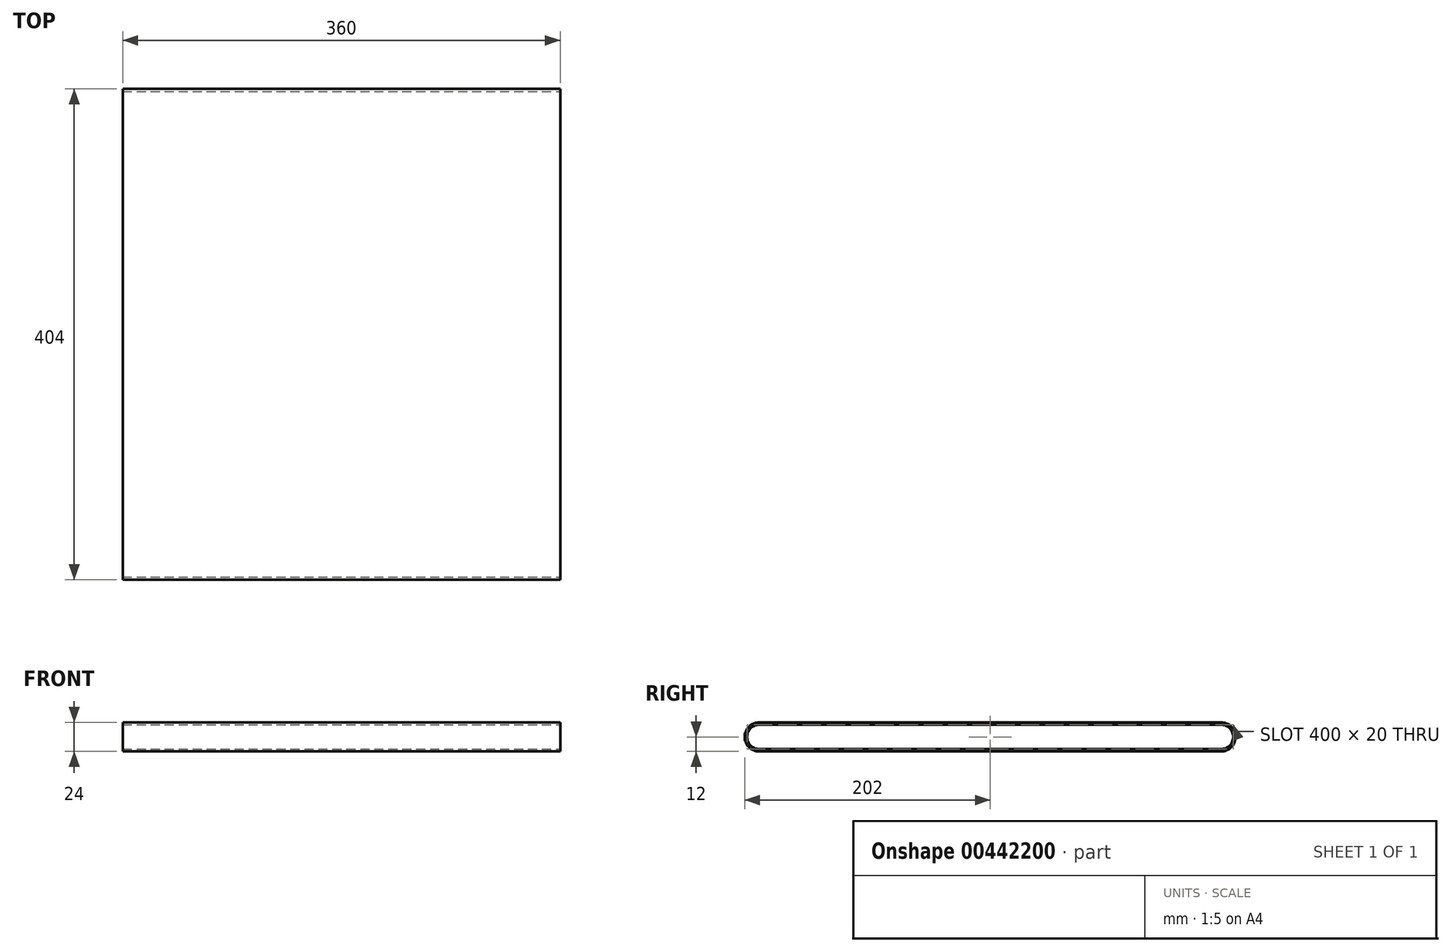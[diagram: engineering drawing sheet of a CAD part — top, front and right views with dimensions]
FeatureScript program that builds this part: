
annotation { "Feature Type Name" : "Feature", "Feature Type Description" : "" }
export const myFeature = defineFeature(function(context is Context, id is Id, definition is map)
    precondition{}
    {
        {
            var Q0;
            Q0=qCreatedBy(makeId("Right.planeOp"),FACE);
            var sketch = newSketch(context, id + "F0", { "sketchPlane" : qUnion([Q0])});
            skLineSegment(sketch, "E0", {"start": v(0, 0) * mm, "end": v(380, 0) * mm});
            skArc(sketch, "E1", {"start": v(380, 0) * mm, "mid": v(390, 10) * mm, "end": v(380, 20) * mm});
            skLineSegment(sketch, "E2", {"start": v(380, 20) * mm, "end": v(0, 20) * mm});
            skArc(sketch, "E3", {"start": v(0, 20) * mm, "mid": v(-10, 10) * mm, "end": v(0, 0) * mm});
            skLineSegment(sketch, "E4", {"start": v(0, 22) * mm, "end": v(380, 22) * mm});
            skLineSegment(sketch, "E5", {"start": v(0, -2) * mm, "end": v(380, -2) * mm});
            skArc(sketch, "E6", {"start": v(0, 22) * mm, "mid": v(-12, 10) * mm, "end": v(0, -2) * mm});
            skArc(sketch, "E7", {"start": v(380, -2) * mm, "mid": v(392, 10) * mm, "end": v(380, 22) * mm});
            skSolve(sketch);
        }
        {
            var Q0;
            Q0=makeQuery(id+"F0.imprint","IMPRINT",FACE,{"disambiguationData":[TD([[makeQuery(id+"F0.imprint","IMPRINT",EDGE,{"derivedFrom":sQuery(id+"F0.wireOp",EDGE,"E0")}),-1.0]])]});
            extrude(context, id + "F1", {"entities" : qUnion([Q0]), "oppositeDirection" : true, "depth" : 360 * mm});
        }
    });
